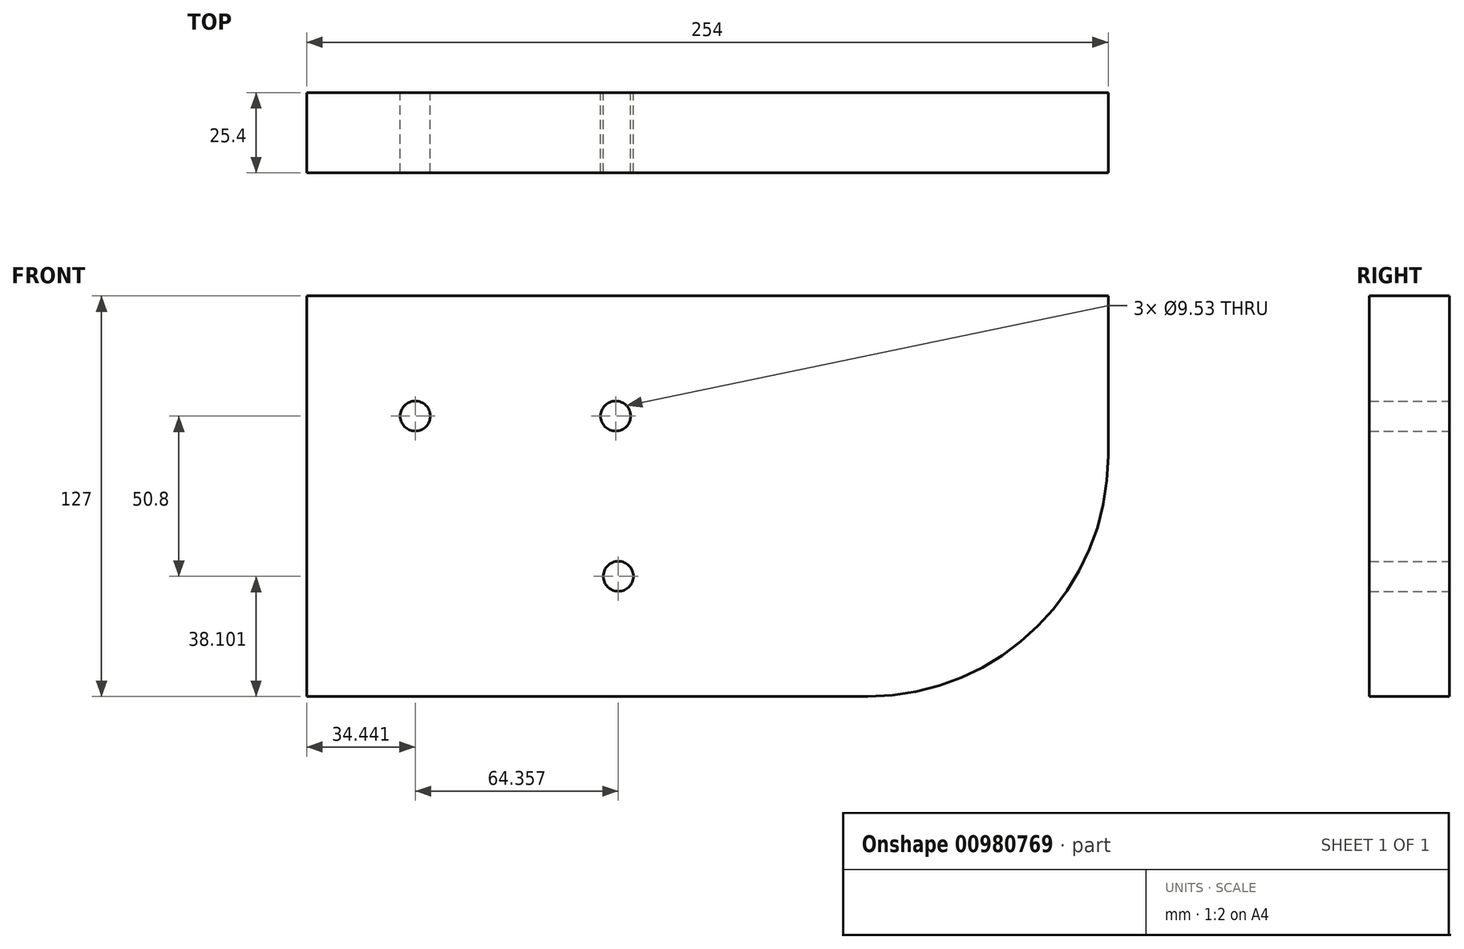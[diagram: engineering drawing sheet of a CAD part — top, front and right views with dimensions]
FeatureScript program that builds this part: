
annotation { "Feature Type Name" : "Feature", "Feature Type Description" : "" }
export const myFeature = defineFeature(function(context is Context, id is Id, definition is map)
    precondition{}
    {
        {
            var Q0;
            Q0=qCreatedBy(makeId("Front.planeOp"),FACE);
            var sketch = newSketch(context, id + "F0", { "sketchPlane" : qUnion([Q0])});
            skLineSegment(sketch, "E0.bottom", {"start": v(-175.17, -431.1) * mm, "end": v(78.83, -431.1) * mm});
            skLineSegment(sketch, "E0.top", {"start": v(-175.17, -558.1) * mm, "end": v(2.63, -558.1) * mm});
            skLineSegment(sketch, "E0.left", {"start": v(-175.17, -431.1) * mm, "end": v(-175.17, -558.1) * mm});
            skLineSegment(sketch, "E0.right", {"start": v(78.83, -431.1) * mm, "end": v(78.83, -481.9) * mm});
            skCircle(sketch, "E1", {"center": v(-140.73, -469.2) * mm, "radius": 4.76 * mm});
            skCircle(sketch, "E2", {"center": v(-77.23, -469.2) * mm, "radius": 4.76 * mm});
            skCircle(sketch, "E3", {"center": v(-76.37, -520) * mm, "radius": 4.76 * mm});
            skPoint(sketch, "E4.visualSharp", {"position": v(78.83, -558.1) * mm});
            skArc(sketch, "E4.filletArc", {"start": v(2.63, -558.1) * mm, "mid": v(56.51, -535.78) * mm, "end": v(78.83, -481.9) * mm});
            skSolve(sketch);
        }
        {
            var Q0;
            Q0 = qSketchRegion(id + "F0", true);
            extrude(context, id + "F1", {"entities" : qUnion([Q0]), "depth" : 25.4 * mm, "offsetDistance" : 25.4 * mm});
        }
    });
